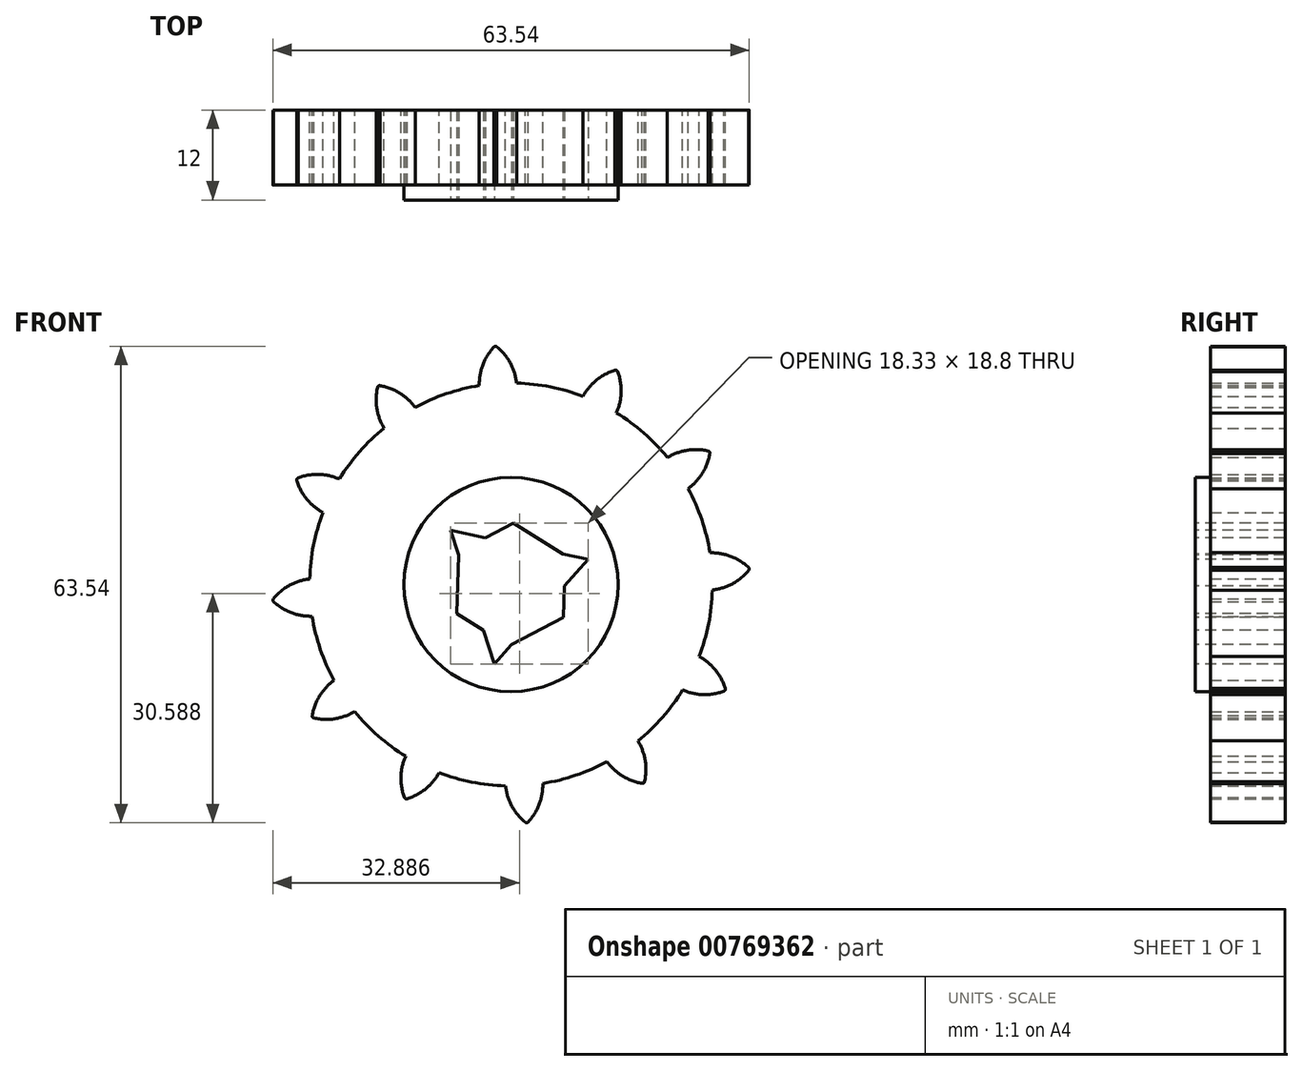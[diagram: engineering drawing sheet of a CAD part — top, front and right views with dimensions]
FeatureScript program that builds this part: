
annotation { "Feature Type Name" : "Feature", "Feature Type Description" : "" }
export const myFeature = defineFeature(function(context is Context, id is Id, definition is map)
    precondition{}
    {
        {
            var Q0;
            Q0=qCreatedBy(makeId("Front.planeOp"),FACE);
            var sketch = newSketch(context, id + "F0", { "sketchPlane" : qUnion([Q0])});
            skCircle(sketch, "E0", {"center": v(0, 0) * mm, "radius": 26.86 * mm});
            skCircle(sketch, "E1", {"center": v(0, 0) * mm, "radius": 29.34 * mm, "construction": true});
            skCircle(sketch, "E2", {"center": v(0, 0) * mm, "radius": 31.75 * mm, "construction": true});
            skLineSegment(sketch, "E3", {"start": v(0, 0) * mm, "end": v(0, 39.49) * mm, "construction": true});
            skLineSegment(sketch, "E4", {"start": v(0, 0) * mm, "end": v(-2.65, 40.47) * mm, "construction": true});
            skLineSegment(sketch, "E5", {"start": v(0, 29.34) * mm, "end": v(-32.88, 27.2) * mm, "construction": true});
            skLineSegment(sketch, "E6", {"start": v(0, 29.34) * mm, "end": v(-27.33, 17.33) * mm, "construction": true});
            skCircle(sketch, "E7", {"center": v(0, 29.34) * mm, "radius": 7.3 * mm, "construction": true});
            skCircle(sketch, "E8", {"center": v(0, 0) * mm, "radius": 26.86 * mm, "construction": true});
            skCircle(sketch, "E9", {"center": v(-6.52, 26.06) * mm, "radius": 7.3 * mm, "construction": true});
            skArc(sketch, "E10", {"start": v(0, 29.34) * mm, "mid": v(-0.82, 30.62) * mm, "end": v(-1.88, 31.7) * mm});
            skArc(sketch, "E11", {"start": v(0.74, 26.85) * mm, "mid": v(0.48, 28.13) * mm, "end": v(0, 29.34) * mm});
            skArc(sketch, "E12.MirrorCS", {"start": v(-3.83, 29.09) * mm, "mid": v(-3.19, 30.46) * mm, "end": v(-2.27, 31.67) * mm});
            skArc(sketch, "E13.MirrorCS", {"start": v(-4.23, 26.52) * mm, "mid": v(-4.14, 27.82) * mm, "end": v(-3.83, 29.09) * mm});
            skArc(sketch, "E14", {"start": v(-1.88, 31.7) * mm, "mid": v(-2.08, 31.77) * mm, "end": v(-2.27, 31.67) * mm});
            skSolve(sketch);
        }
        {
            var Q0;
            {var subQ0=sQuery(id+"F0.wireOp",EDGE,"E0");var subQ1=makeQuery(id+"F0.imprint","INTERSECT",VERTEX,{"derivedFrom":[subQ0,sQuery(id+"F0.wireOp",EDGE,"E11")]});Q0=makeQuery(id+"F0.imprint","IMPRINT",FACE,{"disambiguationData":[TD([[makeQuery(id+"F0.imprint","IMPRINT",EDGE,{"disambiguationData":[TD([[subQ1,-1.0]])],"derivedFrom":subQ0}),1.0]])]});}
            var Q1;
            Q1=makeQuery(id+"F0.imprint","IMPRINT",FACE,{"disambiguationData":[TD([[makeQuery(id+"F0.imprint","IMPRINT",EDGE,{"derivedFrom":sQuery(id+"F0.wireOp",EDGE,"E10")}),1.0]])]});
            extrude(context, id + "F1", {"entities" : qUnion([Q0, Q1]), "depth" : 10 * mm, "offsetDistance" : 25 * mm});
        }
        {
            var Q0;
            Q0=makeQuery(id+"F1.opExtrude","SWEPT_BODY",BODY,{"disambiguationData":[OSD([sQuery(id+"F0.wireOp",EDGE,"E0"),sQuery(id+"F0.wireOp",EDGE,"E10"),sQuery(id+"F0.wireOp",EDGE,"E11"),sQuery(id+"F0.wireOp",EDGE,"E12.MirrorCS"),sQuery(id+"F0.wireOp",EDGE,"E13.MirrorCS"),sQuery(id+"F0.wireOp",EDGE,"E14")])]});
            var Q1;
            Q1=makeQuery(id+"F1.opExtrude","SWEPT_FACE",FACE,{"disambiguationData":[OSD([sQuery(id+"F0.wireOp",EDGE,"E0")])]});
            circularPattern(context, id + "F2", {"operationType" : NewBodyOperationType.ADD, "entities" : qUnion([Q0]), "axis" : qUnion([Q1]), "angle" : 360 * degree, "instanceCount" : 12, "oppositeDirection" : true, "equalSpace" : true});
        }
        {
            var Q0;
            Q0=qCreatedBy(makeId("Front.planeOp"),FACE);
            var sketch = newSketch(context, id + "F3", { "sketchPlane" : qUnion([Q0])});
            skCircle(sketch, "E15", {"center": v(0, 0) * mm, "radius": 14.29 * mm});
            skSolve(sketch);
        }
        {
            var Q0;
            Q0=makeQuery(id+"F3.imprint","IMPRINT",FACE,{"disambiguationData":[TD([[makeQuery(id+"F3.imprint","IMPRINT",EDGE,{"derivedFrom":sQuery(id+"F3.wireOp",EDGE,"E15")}),1.0]])]});
            extrude(context, id + "F4", {"entities" : qUnion([Q0]), "operationType" : NewBodyOperationType.ADD, "depth" : 12 * mm, "offsetDistance" : 25 * mm});
        }
        {
            var Q0;
            Q0=makeQuery(id+"F4.opExtrude","CAP_FACE",FACE,{"disambiguationData":[OSD([sQuery(id+"F3.wireOp",EDGE,"E15")])],"isStart":false});
            var sketch = newSketch(context, id + "F5", { "sketchPlane" : qUnion([Q0])});
            skCircle(sketch, "E16.cCircle", {"center": v(0, 0) * mm, "radius": 7.12 * mm, "construction": true});
            skLineSegment(sketch, "E16.0", {"start": v(0.3, 8.22) * mm, "end": v(7.27, 3.85) * mm});
            skLineSegment(sketch, "E16.1", {"start": v(7.27, 3.85) * mm, "end": v(6.97, -4.37) * mm});
            skLineSegment(sketch, "E16.2", {"start": v(6.97, -4.37) * mm, "end": v(-0.3, -8.22) * mm});
            skLineSegment(sketch, "E16.3", {"start": v(-0.3, -8.22) * mm, "end": v(-7.27, -3.85) * mm});
            skLineSegment(sketch, "E16.4", {"start": v(-7.27, -3.85) * mm, "end": v(-6.97, 4.37) * mm});
            skLineSegment(sketch, "E16.5", {"start": v(-6.97, 4.37) * mm, "end": v(0.3, 8.22) * mm});
            skPoint(sketch, "E16.0.midPoint", {"position": v(3.78, 6.04) * mm});
            skCircle(sketch, "E17.cCircle", {"center": v(0, 0) * mm, "radius": 5.4 * mm, "construction": true});
            skLineSegment(sketch, "E17.0", {"start": v(-8.05, 7.22) * mm, "end": v(10.28, 3.36) * mm});
            skLineSegment(sketch, "E17.1", {"start": v(10.28, 3.36) * mm, "end": v(-2.23, -10.58) * mm});
            skLineSegment(sketch, "E17.2", {"start": v(-2.23, -10.58) * mm, "end": v(-8.05, 7.22) * mm});
            skPoint(sketch, "E17.0.midPoint", {"position": v(1.12, 5.3) * mm});
            skSolve(sketch);
        }
        {
            var Q0;
            {var subQ5=sQuery(id+"F5.wireOp",EDGE,"E16.1");var subQ7=sQuery(id+"F5.wireOp",EDGE,"E16.0");var subQ8=makeQuery(id+"F5.imprint","INTERSECT",VERTEX,{"derivedFrom":[subQ7,subQ5]});Q0=makeQuery(id+"F5.imprint","IMPRINT",FACE,{"disambiguationData":[TD([[makeQuery(id+"F5.imprint","IMPRINT",EDGE,{"disambiguationData":[TD([[subQ8,1.0]])],"derivedFrom":subQ7}),-1.0]])]});}
            var Q1;
            {var subQ0=sQuery(id+"F5.wireOp",EDGE,"E16.5");var subQ1=sQuery(id+"F5.wireOp",EDGE,"E16.0");var subQ2=makeQuery(id+"F5.imprint","INTERSECT",VERTEX,{"derivedFrom":[subQ1,subQ0]});Q1=makeQuery(id+"F5.imprint","IMPRINT",FACE,{"disambiguationData":[TD([[makeQuery(id+"F5.imprint","IMPRINT",EDGE,{"disambiguationData":[TD([[subQ2,-1.0]])],"derivedFrom":subQ1}),-1.0]])]});}
            var Q2;
            {var subQ0=sQuery(id+"F5.wireOp",EDGE,"E16.2");var subQ1=sQuery(id+"F5.wireOp",EDGE,"E16.1");var subQ2=makeQuery(id+"F5.imprint","INTERSECT",VERTEX,{"derivedFrom":[subQ1,subQ0]});Q2=makeQuery(id+"F5.imprint","IMPRINT",FACE,{"disambiguationData":[TD([[makeQuery(id+"F5.imprint","IMPRINT",EDGE,{"disambiguationData":[TD([[subQ2,1.0]])],"derivedFrom":subQ1}),-1.0]])]});}
            var Q3;
            {var subQ0=sQuery(id+"F5.wireOp",EDGE,"E16.4");var subQ1=sQuery(id+"F5.wireOp",EDGE,"E16.3");var subQ2=makeQuery(id+"F5.imprint","INTERSECT",VERTEX,{"derivedFrom":[subQ1,subQ0]});Q3=makeQuery(id+"F5.imprint","IMPRINT",FACE,{"disambiguationData":[TD([[makeQuery(id+"F5.imprint","IMPRINT",EDGE,{"disambiguationData":[TD([[subQ2,1.0]])],"derivedFrom":subQ1}),-1.0]])]});}
            var Q4;
            {var subQ0=sQuery(id+"F5.wireOp",EDGE,"E16.5");var subQ1=sQuery(id+"F5.wireOp",EDGE,"E16.4");var subQ2=makeQuery(id+"F5.imprint","INTERSECT",VERTEX,{"derivedFrom":[subQ1,subQ0]});Q4=makeQuery(id+"F5.imprint","IMPRINT",FACE,{"disambiguationData":[TD([[makeQuery(id+"F5.imprint","IMPRINT",EDGE,{"disambiguationData":[TD([[subQ2,1.0]])],"derivedFrom":subQ1}),1.0]])]});}
            var Q5;
            {var subQ0=sQuery(id+"F5.wireOp",EDGE,"E16.3");var subQ1=sQuery(id+"F5.wireOp",EDGE,"E16.2");var subQ2=makeQuery(id+"F5.imprint","INTERSECT",VERTEX,{"derivedFrom":[subQ1,subQ0]});Q5=makeQuery(id+"F5.imprint","IMPRINT",FACE,{"disambiguationData":[TD([[makeQuery(id+"F5.imprint","IMPRINT",EDGE,{"disambiguationData":[TD([[subQ2,1.0]])],"derivedFrom":subQ1}),1.0]])]});}
            var Q6;
            {var subQ0=sQuery(id+"F5.wireOp",EDGE,"E16.1");var subQ1=sQuery(id+"F5.wireOp",EDGE,"E16.0");var subQ2=makeQuery(id+"F5.imprint","INTERSECT",VERTEX,{"derivedFrom":[subQ1,subQ0]});Q6=makeQuery(id+"F5.imprint","IMPRINT",FACE,{"disambiguationData":[TD([[makeQuery(id+"F5.imprint","IMPRINT",EDGE,{"disambiguationData":[TD([[subQ2,1.0]])],"derivedFrom":subQ1}),1.0]])]});}
            extrude(context, id + "F6", {"entities" : qUnion([Q0, Q1, Q2, Q3, Q4, Q5, Q6]), "operationType" : NewBodyOperationType.REMOVE, "oppositeDirection" : true, "depth" : 25 * mm, "offsetDistance" : 25 * mm});
        }
    });
